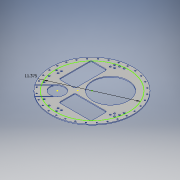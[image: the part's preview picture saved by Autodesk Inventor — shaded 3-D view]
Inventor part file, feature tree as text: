
AUTODESK INVENTOR PART (.ipt)
format: ipt  version: 2018 (Build 220112000, 112)  size: 324,096 bytes
history: native  units: in
note: dims shown in document units (in); Inventor stores cm internally (conversion verified against a paired STEP export)
features: sketch x8, extrude x4, hole x4, pattern_circular x1, fillet x1
ambient origin geometry x8: Origin, YZ Plane, XZ Plane, XY Plane, X Axis, Y Axis, Z Axis, Center Point
bodies: Solid1 (feature_tree)
feature tree (18):
  extrude  "Extrusion1"  TaperAngle=135.0deg  [1 undecoded]
  extrude  "Extrusion2"  Depth=2.25in
  hole  "Hole3"  [1 undecoded]
  pattern_circular  "Circular Pattern1"  [2 undecoded]
  hole  "Hole5"  [1 undecoded]
  hole  "Hole6"  [1 undecoded]
  extrude  "Extrusion3"  Depth=0.25in
  fillet  "Fillet1"  Radius=0.2749in
  sketch  "Sketch15"  dims[d8=12.75in]
  extrude  "Extrusion4"  Depth=0.25in
  hole  "Hole9"  [1 undecoded]
  sketch  "Sketch1"  dims[d0=3.6in d1=135.0deg]
  sketch  "Sketch2"  dims[d2=5.5in d3=2.25in]
  sketch  "Sketch6"  dims[d4=45.0deg d5=2.27in]
  sketch  "Sketch11"  dims[d6=1.56in]
  sketch  "Sketch13"  dims[d7=315.0deg]
  sketch  "Sketch17"  dims[d9=0.125in d10=0.0in]
  sketch  "Sketch19"  dims[d11=0.0in d12=0.0in d65=6.1in d66=0.0344in d67=0.196in d68=0.5in d69=0.375in d70=0.25in d71=0.5635in d72=0.75in d73=0.8108in d74=12.5984in d75=360.0deg d97=8.5in d98=0.2749in d99=8.5in d100=0.3436in d101=9.708in d102=9.708in d103=1.5748in d105=360.0deg d109=7.75in d110=0.962in d111=7.75in d112=0.8933in d116=0.266in d117=0.75in d118=0.507in d119=0.25in d120=0.5635in d121=1.0in d122=0.8108in d132=0.266in d133=0.75in d134=0.507in d135=0.25in d136=0.5635in d137=1.0in d138=0.8108in d147=11.0in d148=9.708in d149=9.708in d150=5.5in d152=5.5in d153=5.5in d154=5.5in d155=5.0in d156=90.0deg d157=2.5in d160=1.0in d161=45.0deg d162=1.0in d163=0.0in d164=2.9in d165=180.0deg d166=1.5in d167=90.0deg d168=0.25in d171=11.375in d180=0.1in d181=0.1in d182=1.0in d183=0.0in d201=10.0in d204=0.266in d205=0.75in d206=0.507in d207=0.25in d208=0.5635in d209=1.0in d210=0.8108in d212=1.0in d213=45.0deg d215=0.0206in d216=0.0206in]
note: 7 required parameter values undecoded (feature->parameter linkage not recoverable at this tier; creation-order binding heuristic only, values carry confidence <= 0.55)
